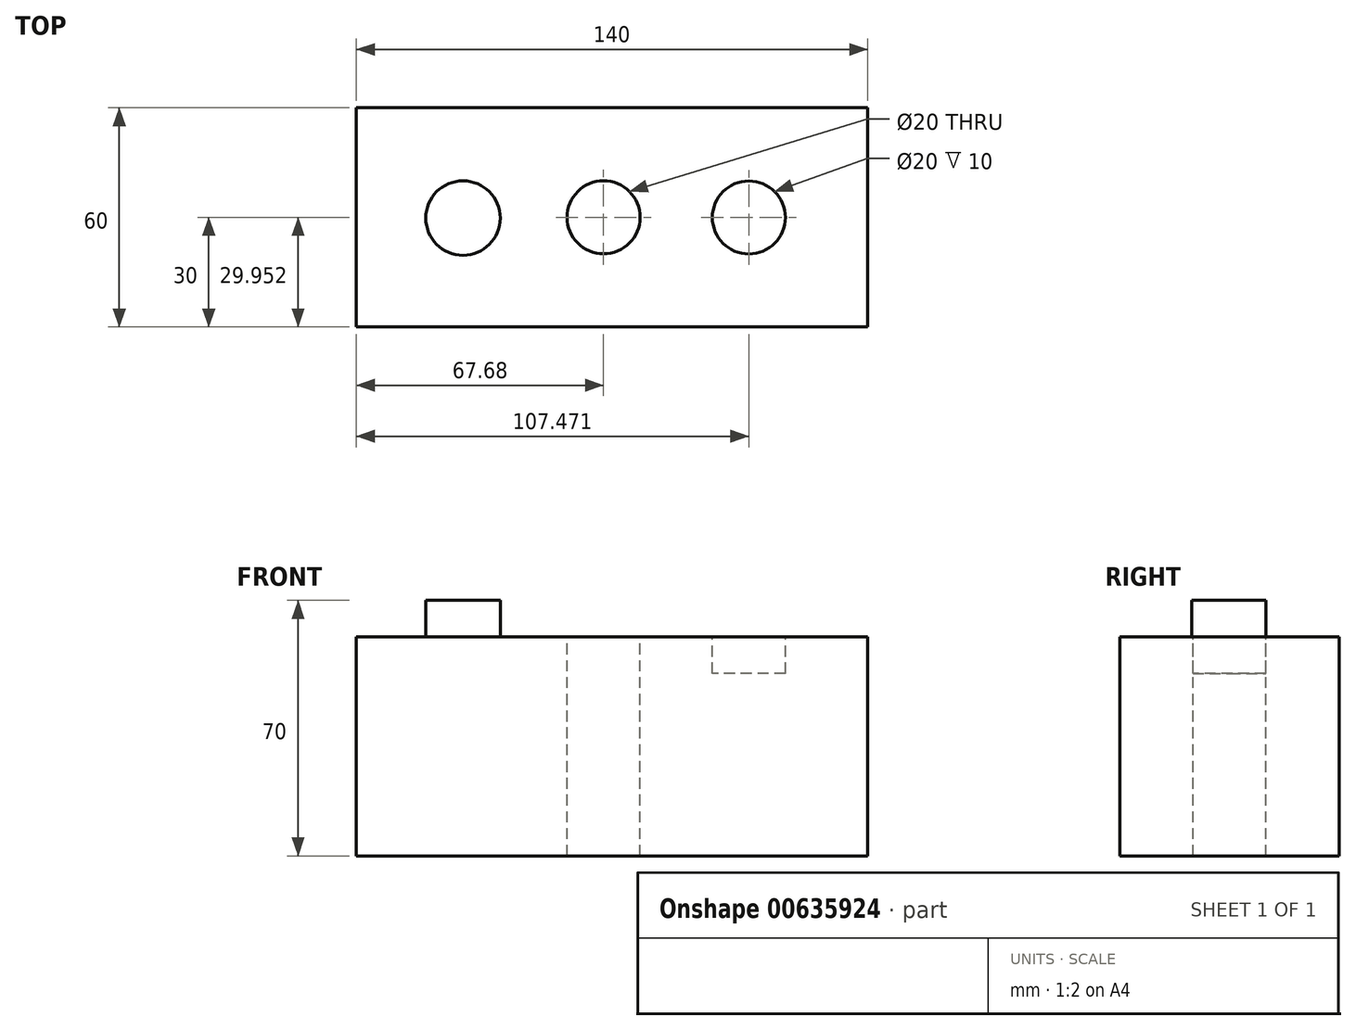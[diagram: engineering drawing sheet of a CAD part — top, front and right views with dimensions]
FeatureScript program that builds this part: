
annotation { "Feature Type Name" : "Feature", "Feature Type Description" : "" }
export const myFeature = defineFeature(function(context is Context, id is Id, definition is map)
    precondition{}
    {
        {
            var Q0;
            Q0=qCreatedBy(makeId("Top.planeOp"),FACE);
            var sketch = newSketch(context, id + "F0", { "sketchPlane" : qUnion([Q0])});
            skLineSegment(sketch, "E0.bottom", {"start": v(72.32, -30) * mm, "end": v(-67.68, -30) * mm});
            skLineSegment(sketch, "E0.top", {"start": v(72.32, 30) * mm, "end": v(-67.68, 30) * mm});
            skLineSegment(sketch, "E0.left", {"start": v(72.32, -30) * mm, "end": v(72.32, 30) * mm});
            skLineSegment(sketch, "E0.right", {"start": v(-67.68, -30) * mm, "end": v(-67.68, 30) * mm});
            skPoint(sketch, "E0.middle", {"position": v(2.32, 0) * mm});
            skSolve(sketch);
        }
        {
            var Q0;
            Q0 = qSketchRegion(id + "F0", true);
            extrude(context, id + "F1", {"entities" : qUnion([Q0]), "depth" : 60 * mm, "offsetDistance" : 25 * mm});
        }
        {
            var Q0;
            Q0=makeQuery(id+"F1.opExtrude","CAP_FACE",FACE,{"disambiguationData":[OSD([sQuery(id+"F0.wireOp",EDGE,"E0.bottom"),sQuery(id+"F0.wireOp",EDGE,"E0.top"),sQuery(id+"F0.wireOp",EDGE,"E0.left"),sQuery(id+"F0.wireOp",EDGE,"E0.right")])],"isStart":false});
            var sketch = newSketch(context, id + "F2", { "sketchPlane" : qUnion([Q0])});
            skLineSegment(sketch, "E1", {"start": v(-67.68, 0) * mm, "end": v(-48, 0) * mm});
            skPoint(sketch, "E1.endSnap0", {"position": v(-67.68, 0) * mm});
            skSolve(sketch);
        }
        {
            var Q0;
            {var subQ1=makeQuery(id+"F1.opExtrude","CAP_EDGE",EDGE,{"disambiguationData":[OSD([sQuery(id+"F0.wireOp",EDGE,"E0.bottom")])],"isStart":false});Q0=makeQuery(id+"F2.imprint","IMPRINT",FACE,{"disambiguationData":[TD([[makeQuery(id+"F2.imprint","IMPRINT",EDGE,{"derivedFrom":subQ1}),-1.0]])]});}
            var sketch = newSketch(context, id + "F3", { "sketchPlane" : qUnion([Q0])});
            skCircle(sketch, "E2", {"center": v(-38.5, -0.21) * mm, "radius": 10.21 * mm});
            skPoint(sketch, "E2.first.point", {"position": v(-48.7, 0) * mm});
            skPoint(sketch, "E2.second.point", {"position": v(-28.29, 0) * mm});
            skPoint(sketch, "E2.third.point", {"position": v(-38.78, 10) * mm});
            skSolve(sketch);
        }
        {
            var Q0;
            {var subQ1=makeQuery(id+"F1.opExtrude","CAP_EDGE",EDGE,{"disambiguationData":[OSD([sQuery(id+"F0.wireOp",EDGE,"E0.bottom")])],"isStart":false});Q0=makeQuery(id+"F2.imprint","IMPRINT",FACE,{"disambiguationData":[TD([[makeQuery(id+"F2.imprint","IMPRINT",EDGE,{"derivedFrom":subQ1}),-1.0]])]});}
            var sketch = newSketch(context, id + "F4", { "sketchPlane" : qUnion([Q0])});
            skCircle(sketch, "E3", {"center": v(0, 0) * mm, "radius": 10 * mm});
            skSolve(sketch);
        }
        {
            var Q0;
            {var subQ1=makeQuery(id+"F1.opExtrude","CAP_EDGE",EDGE,{"disambiguationData":[OSD([sQuery(id+"F0.wireOp",EDGE,"E0.bottom")])],"isStart":false});Q0=makeQuery(id+"F2.imprint","IMPRINT",FACE,{"disambiguationData":[TD([[makeQuery(id+"F2.imprint","IMPRINT",EDGE,{"derivedFrom":subQ1}),-1.0]])]});}
            var sketch = newSketch(context, id + "F5", { "sketchPlane" : qUnion([Q0])});
            skCircle(sketch, "E4", {"center": v(39.8, -0.05) * mm, "radius": 10 * mm});
            skPoint(sketch, "E4.first.point", {"position": v(49.8, 0) * mm});
            skPoint(sketch, "E4.second.point", {"position": v(29.8, 0) * mm});
            skPoint(sketch, "E4.third.point", {"position": v(34.51, -8.54) * mm});
            skSolve(sketch);
        }
        {
            var Q0;
            Q0=makeQuery(id+"F3.imprint","IMPRINT",FACE,{"disambiguationData":[TD([[makeQuery(id+"F3.imprint","IMPRINT",EDGE,{"derivedFrom":sQuery(id+"F3.wireOp",EDGE,"E2")}),1.0]])]});
            var Q1;
            Q1 = qSketchRegion(id + "F3", true);
            extrude(context, id + "F6", {"entities" : qUnion([Q0, Q1]), "operationType" : NewBodyOperationType.ADD, "depth" : 10 * mm, "offsetDistance" : 25 * mm});
        }
        {
            var Q0;
            Q0 = qSketchRegion(id + "F4", true);
            extrude(context, id + "F7", {"entities" : qUnion([Q0]), "operationType" : NewBodyOperationType.REMOVE, "oppositeDirection" : true, "depth" : 110.6 * mm, "offsetDistance" : 25 * mm});
        }
        {
            var Q0;
            Q0 = qSketchRegion(id + "F5", true);
            extrude(context, id + "F8", {"entities" : qUnion([Q0]), "operationType" : NewBodyOperationType.REMOVE, "oppositeDirection" : true, "depth" : 10 * mm, "offsetDistance" : 25 * mm});
        }
    });
